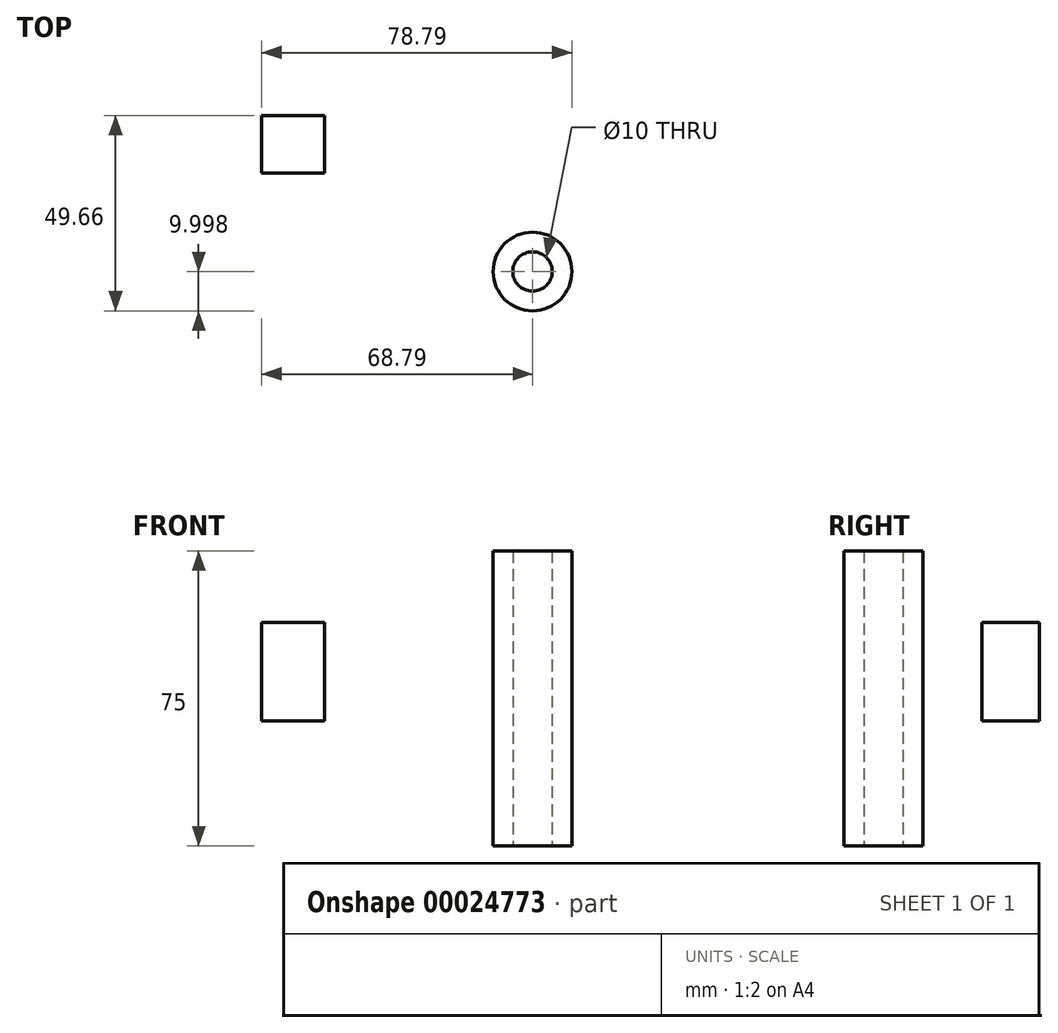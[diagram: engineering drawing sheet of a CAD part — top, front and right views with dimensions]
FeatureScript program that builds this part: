
annotation { "Feature Type Name" : "Feature", "Feature Type Description" : "" }
export const myFeature = defineFeature(function(context is Context, id is Id, definition is map)
    precondition{}
    {
        {
            var Q0;
            Q0=qCreatedBy(makeId("Front.planeOp"),FACE);
            var sketch = newSketch(context, id + "F0", { "sketchPlane" : qUnion([Q0])});
            skCircle(sketch, "E0", {"center": v(0, 0) * mm, "radius": 10 * mm});
            skCircle(sketch, "E1", {"center": v(0, 0) * mm, "radius": 5 * mm});
            skSolve(sketch);
        }
        {
            var Q0;
            Q0=makeQuery(id+"F0.imprint","IMPRINT",FACE,{"disambiguationData":[TD([[makeQuery(id+"F0.imprint","IMPRINT",EDGE,{"derivedFrom":sQuery(id+"F0.wireOp",EDGE,"E0")}),1.0]])]});
            extrude(context, id + "F1", {"entities" : qUnion([Q0]), "depth" : 75 * mm});
        }
        {
            var Q0;
            Q0=qCreatedBy(makeId("Top.planeOp"),FACE);
            var sketch = newSketch(context, id + "F2", { "sketchPlane" : qUnion([Q0])});
            skLineSegment(sketch, "E2.bottom", {"start": v(-52.88, -56.86) * mm, "end": v(-68.8, -56.86) * mm});
            skLineSegment(sketch, "E2.top", {"start": v(-52.88, -42.2) * mm, "end": v(-68.8, -42.2) * mm});
            skLineSegment(sketch, "E2.left", {"start": v(-52.88, -56.86) * mm, "end": v(-52.88, -42.2) * mm});
            skLineSegment(sketch, "E2.right", {"start": v(-68.8, -56.86) * mm, "end": v(-68.8, -42.2) * mm});
            skSolve(sketch);
        }
        {
            var Q0;
            Q0=makeQuery(id+"F2.imprint","IMPRINT",FACE,{"disambiguationData":[TD([[makeQuery(id+"F2.imprint","IMPRINT",EDGE,{"derivedFrom":sQuery(id+"F2.wireOp",EDGE,"E2.bottom")}),-1.0]])]});
            extrude(context, id + "F3", {"entities" : qUnion([Q0]), "depth" : 25 * mm});
        }
        {
            var Q0;
            Q0=makeQuery(id+"F1.opExtrude","SWEPT_BODY",BODY,{"disambiguationData":[OSD([sQuery(id+"F0.wireOp",EDGE,"E0"),sQuery(id+"F0.wireOp",EDGE,"E1")])]});
            var Q1;
            Q1=makeQuery(id+"F3.opExtrude","CAP_EDGE",EDGE,{"disambiguationData":[OSD([sQuery(id+"F2.wireOp",EDGE,"E2.bottom")])],"isStart":false});
            transform(context, id + "F4", {"entities" : qUnion([Q0]), "transformType" : TransformType.ROTATION, "transformAxis" : qUnion([Q1]), "angle" : 90 * degree, "makeCopy" : false});
        }
    });
